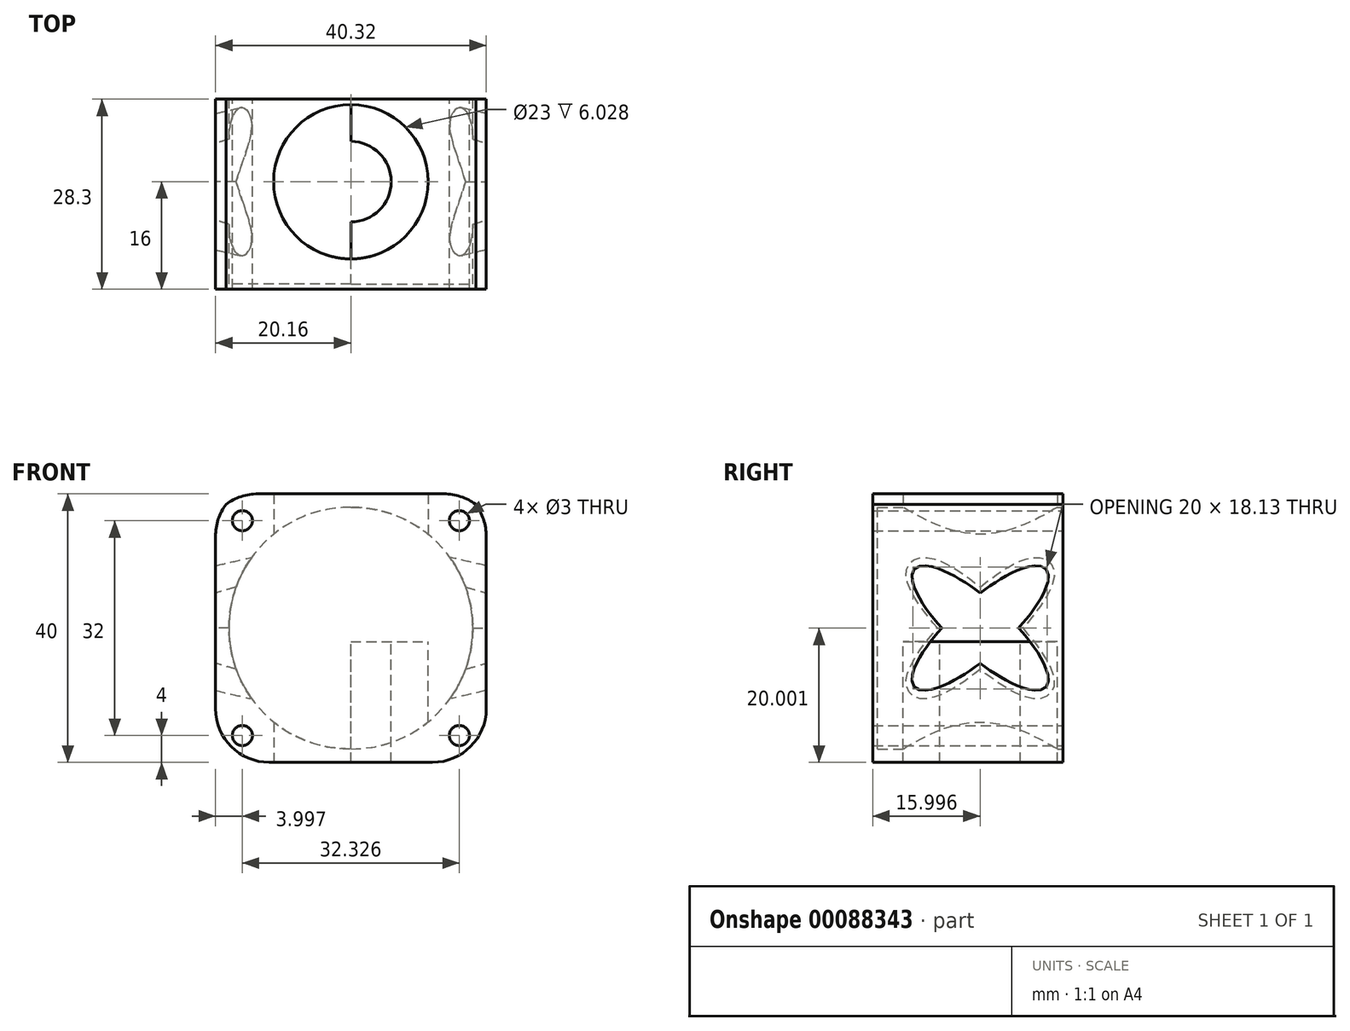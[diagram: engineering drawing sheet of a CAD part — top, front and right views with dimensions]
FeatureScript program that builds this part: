
annotation { "Feature Type Name" : "Feature", "Feature Type Description" : "" }
export const myFeature = defineFeature(function(context is Context, id is Id, definition is map)
    precondition{}
    {
        {
            var Q0;
            Q0=qCreatedBy(makeId("Top.planeOp"),FACE);
            var sketch = newSketch(context, id + "F11", { "sketchPlane" : qUnion([Q0])});
            skCircle(sketch, "E0", {"center": v(0, 0) * mm, "radius": 8 * mm});
            skCircle(sketch, "E1.cCircle", {"center": v(0, 0) * mm, "radius": 11.5 * mm, "construction": true});
            skLineSegment(sketch, "E1.0", {"start": v(11.5, 11.5) * mm, "end": v(11.5, -11.5) * mm});
            skLineSegment(sketch, "E1.1", {"start": v(11.5, -11.5) * mm, "end": v(-11.5, -11.5) * mm});
            skLineSegment(sketch, "E1.2", {"start": v(-11.5, -11.5) * mm, "end": v(-11.5, 11.5) * mm});
            skLineSegment(sketch, "E1.3", {"start": v(-11.5, 11.5) * mm, "end": v(11.5, 11.5) * mm});
            skPoint(sketch, "E1.0.midPoint", {"position": v(11.5, 0) * mm});
            skPoint(sketch, "E2.0.midPoint", {"position": v(0, 36.09) * mm});
            skPoint(sketch, "E3", {"position": v(0, -11.5) * mm});
            skLineSegment(sketch, "E4.MirrorCS", {"start": v(0, 12.3) * mm, "end": v(-20.16, 12.3) * mm});
            skLineSegment(sketch, "E5.MirrorCS", {"start": v(-20.16, 16) * mm, "end": v(-20.16, 0) * mm});
            skLineSegment(sketch, "E6.MirrorCS", {"start": v(0, -16) * mm, "end": v(-20.16, -16) * mm});
            skCircle(sketch, "E7", {"center": v(0, 0) * mm, "radius": 6 * mm});
            skCircle(sketch, "E8", {"center": v(0, 0) * mm, "radius": 11.5 * mm});
            skPoint(sketch, "E9.0.midPoint", {"position": v(0, -12.5) * mm});
            skLineSegment(sketch, "E10.0", {"start": v(-16.45, 9.5) * mm, "end": v(16.45, 9.5) * mm, "construction": true});
            skLineSegment(sketch, "E10.1", {"start": v(16.45, 9.5) * mm, "end": v(0, -19) * mm, "construction": true});
            skLineSegment(sketch, "E10.2", {"start": v(0, -19) * mm, "end": v(-16.45, 9.5) * mm, "construction": true});
            skPoint(sketch, "E10.0.midPoint", {"position": v(0, 9.5) * mm});
            skCircle(sketch, "E11", {"center": v(-16.45, 9.5) * mm, "radius": 1.5 * mm});
            skCircle(sketch, "E12", {"center": v(16.45, 9.5) * mm, "radius": 1.5 * mm});
            skCircle(sketch, "E13", {"center": v(0, -19) * mm, "radius": 1.5 * mm});
            skLineSegment(sketch, "E14", {"start": v(-20.16, 0) * mm, "end": v(-20.16, -16) * mm});
            skLineSegment(sketch, "E15", {"start": v(0, 12.3) * mm, "end": v(0, -16) * mm});
            skLineSegment(sketch, "E16.MirrorCS", {"start": v(0, 12.3) * mm, "end": v(20.16, 12.3) * mm});
            skLineSegment(sketch, "E17.MirrorCS", {"start": v(20.16, 16) * mm, "end": v(20.16, 0) * mm});
            skLineSegment(sketch, "E18.MirrorCS", {"start": v(20.16, 0) * mm, "end": v(20.16, -16) * mm});
            skLineSegment(sketch, "E19.MirrorCS", {"start": v(0, -16) * mm, "end": v(20.16, -16) * mm});
            skSolve(sketch);
        }
        {
            var Q0;
            {var subQ14=sQuery(id+"F11.wireOp",EDGE,"E4.MirrorCS");Q0=makeQuery(id+"F11.imprint","IMPRINT",FACE,{"disambiguationData":[TD([[makeQuery(id+"F11.imprint","IMPRINT",EDGE,{"derivedFrom":subQ14}),1.0]])]});}
            var Q1;
            Q1=makeQuery(id+"F11.imprint","IMPRINT",FACE,{"disambiguationData":[TD([[makeQuery(id+"F11.imprint","IMPRINT",EDGE,{"derivedFrom":sQuery(id+"F11.wireOp",EDGE,"E11")}),1.0]])]});
            var Q2;
            {var subQ0=sQuery(id+"F11.wireOp",EDGE,"E1.3");var subQ1=sQuery(id+"F11.wireOp",EDGE,"E1.2");var subQ2=makeQuery(id+"F11.imprint","INTERSECT",VERTEX,{"derivedFrom":[subQ1,subQ0]});Q2=makeQuery(id+"F11.imprint","IMPRINT",FACE,{"disambiguationData":[TD([[makeQuery(id+"F11.imprint","IMPRINT",EDGE,{"disambiguationData":[TD([[subQ2,1.0]])],"derivedFrom":subQ1}),-1.0]])]});}
            var Q3;
            {var subQ0=sQuery(id+"F11.wireOp",EDGE,"E1.2");var subQ1=sQuery(id+"F11.wireOp",EDGE,"E1.1");var subQ2=makeQuery(id+"F11.imprint","INTERSECT",VERTEX,{"derivedFrom":[subQ1,subQ0]});Q3=makeQuery(id+"F11.imprint","IMPRINT",FACE,{"disambiguationData":[TD([[makeQuery(id+"F11.imprint","IMPRINT",EDGE,{"disambiguationData":[TD([[subQ2,-1.0]])],"derivedFrom":subQ0}),-1.0]])]});}
            extrude(context, id + "F0", {"entities" : qUnion([Q0, Q1, Q2, Q3]), "depth" : 22 * mm});
        }
        {
            var Q0;
            {var subQ0=sQuery(id+"F11.wireOp",EDGE,"E1.3");var subQ1=sQuery(id+"F11.wireOp",EDGE,"E1.2");var subQ2=makeQuery(id+"F11.imprint","INTERSECT",VERTEX,{"derivedFrom":[subQ1,subQ0]});Q0=makeQuery(id+"F11.imprint","IMPRINT",FACE,{"disambiguationData":[TD([[makeQuery(id+"F11.imprint","IMPRINT",EDGE,{"disambiguationData":[TD([[subQ2,1.0]])],"derivedFrom":subQ1}),-1.0]])]});}
            var Q1;
            {var subQ14=sQuery(id+"F11.wireOp",EDGE,"E4.MirrorCS");Q1=makeQuery(id+"F11.imprint","IMPRINT",FACE,{"disambiguationData":[TD([[makeQuery(id+"F11.imprint","IMPRINT",EDGE,{"derivedFrom":subQ14}),1.0]])]});}
            var Q2;
            {var subQ0=sQuery(id+"F11.wireOp",EDGE,"E1.2");var subQ1=sQuery(id+"F11.wireOp",EDGE,"E1.1");var subQ2=makeQuery(id+"F11.imprint","INTERSECT",VERTEX,{"derivedFrom":[subQ1,subQ0]});Q2=makeQuery(id+"F11.imprint","IMPRINT",FACE,{"disambiguationData":[TD([[makeQuery(id+"F11.imprint","IMPRINT",EDGE,{"disambiguationData":[TD([[subQ2,-1.0]])],"derivedFrom":subQ0}),-1.0]])]});}
            var Q3;
            Q3=makeQuery(id+"F11.imprint","IMPRINT",FACE,{"disambiguationData":[TD([[makeQuery(id+"F11.imprint","IMPRINT",EDGE,{"derivedFrom":sQuery(id+"F11.wireOp",EDGE,"E11")}),1.0]])]});
            var Q4;
            {var subQ0=sQuery(id+"F11.wireOp",EDGE,"E15");var subQ1=sQuery(id+"F11.wireOp",EDGE,"E0");var subQ2=makeQuery(id+"F11.imprint","INTERSECT",VERTEX,{"disambiguationData":[OD(0.0)],"derivedFrom":[subQ1,subQ0]});Q4=makeQuery(id+"F11.imprint","IMPRINT",FACE,{"disambiguationData":[TD([[makeQuery(id+"F11.imprint","IMPRINT",EDGE,{"disambiguationData":[TD([[subQ2,-1.0]])],"derivedFrom":subQ1}),-1.0]])]});}
            var Q5;
            {var subQ0=sQuery(id+"F11.wireOp",EDGE,"E15");var subQ1=sQuery(id+"F11.wireOp",EDGE,"E0");var subQ2=makeQuery(id+"F11.imprint","INTERSECT",VERTEX,{"disambiguationData":[OD(0.0)],"derivedFrom":[subQ1,subQ0]});Q5=makeQuery(id+"F11.imprint","IMPRINT",FACE,{"disambiguationData":[TD([[makeQuery(id+"F11.imprint","IMPRINT",EDGE,{"disambiguationData":[TD([[subQ2,-1.0]])],"derivedFrom":subQ1}),1.0]])]});}
            extrude(context, id + "F1", {"entities" : qUnion([Q0, Q1, Q2, Q3, Q4, Q5]), "operationType" : NewBodyOperationType.ADD, "oppositeDirection" : true, "depth" : 18 * mm});
        }
        {
            var Q0;
            {var subQ0=sQuery(id+"F11.wireOp",EDGE,"E4.MirrorCS");var subQ1=sQuery(id+"F11.wireOp",EDGE,"b9b2a584-45d9-46e1-b681-84b6f52c41030.MirrorCS");Q0=makeQuery(id+"F1.boolean.opBoolean","MERGE",FACE,{"derivedFrom":[makeQuery(id+"F0.opExtrude","SWEPT_FACE",FACE,{"disambiguationData":[OSD([subQ1,subQ0])]}),makeQuery(id+"F1.opExtrude","SWEPT_FACE",FACE,{"disambiguationData":[OSD([subQ1,subQ0])]})]});}
            var sketch = newSketch(context, id + "F2", { "sketchPlane" : qUnion([Q0])});
            skLineSegment(sketch, "E20.bottom", {"start": v(20.16, 22) * mm, "end": v(20.16, 22) * mm});
            skLineSegment(sketch, "E20.top", {"start": v(20.16, -8) * mm, "end": v(20.16, -8) * mm});
            skLineSegment(sketch, "E20.left", {"start": v(20.16, 22) * mm, "end": v(20.16, -8) * mm});
            skLineSegment(sketch, "E20.right", {"start": v(20.16, 22) * mm, "end": v(20.16, -8) * mm});
            skCircle(sketch, "E21", {"center": v(0.16, 2) * mm, "radius": 18 * mm});
            skLineSegment(sketch, "E22.bottom", {"start": v(-15.84, -14) * mm, "end": v(16.16, -14) * mm, "construction": true});
            skLineSegment(sketch, "E22.top", {"start": v(-15.84, 18) * mm, "end": v(16.16, 18) * mm, "construction": true});
            skLineSegment(sketch, "E22.left", {"start": v(-15.84, -14) * mm, "end": v(-15.84, 18) * mm, "construction": true});
            skLineSegment(sketch, "E22.right", {"start": v(16.16, -14) * mm, "end": v(16.16, 18) * mm, "construction": true});
            skCircle(sketch, "E23", {"center": v(16.16, -14) * mm, "radius": 1.5 * mm});
            skCircle(sketch, "E24", {"center": v(-15.84, -14) * mm, "radius": 1.5 * mm});
            skCircle(sketch, "E25", {"center": v(-15.84, 18) * mm, "radius": 1.5 * mm});
            skCircle(sketch, "E26", {"center": v(16.16, 18) * mm, "radius": 1.5 * mm});
            skSolve(sketch);
        }
        {
            var Q0;
            {var subQ0=sQuery(id+"F2.wireOp",EDGE,"E21");var subQ1=sQuery(id+"F11.wireOp",EDGE,"E16.MirrorCS");var subQ2=sQuery(id+"F11.wireOp",EDGE,"E15");var subQ3=sQuery(id+"F11.wireOp",EDGE,"E4.MirrorCS");var subQ4=makeQuery(id+"F1.boolean.opBoolean","MERGE",EDGE,{"derivedFrom":[makeQuery(id+"F0.opExtrude","SWEPT_EDGE",EDGE,{"disambiguationData":[OSD([subQ3,subQ2,subQ1])]}),makeQuery(id+"F1.opExtrude","SWEPT_EDGE",EDGE,{"disambiguationData":[OSD([subQ3,subQ2,subQ1])]})]});var subQ5=makeQuery(id+"F2.imprint","INTERSECT",VERTEX,{"disambiguationData":[OD(0.0)],"derivedFrom":[subQ4,subQ0]});Q0=makeQuery(id+"F2.imprint","IMPRINT",FACE,{"disambiguationData":[TD([[makeQuery(id+"F2.imprint","IMPRINT",EDGE,{"disambiguationData":[TD([[subQ5,1.0]])],"derivedFrom":subQ0}),1.0]])]});}
            var Q1;
            Q1=makeQuery(id+"F2.imprint","IMPRINT",FACE,{"disambiguationData":[TD([[makeQuery(id+"F2.imprint","IMPRINT",EDGE,{"derivedFrom":sQuery(id+"F2.wireOp",EDGE,"E23")}),1.0]])]});
            var Q2;
            Q2=makeQuery(id+"F2.imprint","IMPRINT",FACE,{"disambiguationData":[TD([[makeQuery(id+"F2.imprint","IMPRINT",EDGE,{"derivedFrom":sQuery(id+"F2.wireOp",EDGE,"E26")}),1.0]])]});
            extrude(context, id + "F3", {"entities" : qUnion([Q0, Q1, Q2]), "operationType" : NewBodyOperationType.REMOVE, "oppositeDirection" : true, "depth" : 27.57 * mm});
        }
        {
            var Q0;
            Q0=makeQuery(id+"F2.imprint","IMPRINT",FACE,{"disambiguationData":[TD([[makeQuery(id+"F2.imprint","IMPRINT",EDGE,{"derivedFrom":sQuery(id+"F2.wireOp",EDGE,"E23")}),1.0]])]});
            var Q1;
            Q1=makeQuery(id+"F2.imprint","IMPRINT",FACE,{"disambiguationData":[TD([[makeQuery(id+"F2.imprint","IMPRINT",EDGE,{"derivedFrom":sQuery(id+"F2.wireOp",EDGE,"E24")}),1.0]])]});
            var Q2;
            Q2=makeQuery(id+"F2.imprint","IMPRINT",FACE,{"disambiguationData":[TD([[makeQuery(id+"F2.imprint","IMPRINT",EDGE,{"derivedFrom":sQuery(id+"F2.wireOp",EDGE,"E26")}),1.0]])]});
            var Q3;
            Q3=makeQuery(id+"F2.imprint","IMPRINT",FACE,{"disambiguationData":[TD([[makeQuery(id+"F2.imprint","IMPRINT",EDGE,{"derivedFrom":sQuery(id+"F2.wireOp",EDGE,"E25")}),1.0]])]});
            extrude(context, id + "F4", {"entities" : qUnion([Q0, Q1, Q2, Q3]), "operationType" : NewBodyOperationType.REMOVE, "oppositeDirection" : true, "depth" : 50 * mm});
        }
        {
            var Q0;
            {var subQ0=sQuery(id+"F11.wireOp",EDGE,"E15");var subQ1=sQuery(id+"F11.wireOp",EDGE,"E0");var subQ2=makeQuery(id+"F11.imprint","INTERSECT",VERTEX,{"disambiguationData":[OD(0.0)],"derivedFrom":[subQ1,subQ0]});Q0=makeQuery(id+"F11.imprint","IMPRINT",FACE,{"disambiguationData":[TD([[makeQuery(id+"F11.imprint","IMPRINT",EDGE,{"disambiguationData":[TD([[subQ2,-1.0]])],"derivedFrom":subQ1}),1.0]])]});}
            extrude(context, id + "F5", {"entities" : qUnion([Q0]), "operationType" : NewBodyOperationType.ADD, "oppositeDirection" : true, "depth" : 16.75 * mm, "hasSecondDirection" : true, "secondDirectionOppositeDirection" : true, "secondDirectionDepth" : 12.5 * mm});
        }
        {
            var Q0;
            {var subQ0=sQuery(id+"F11.wireOp",EDGE,"E14");var subQ1=sQuery(id+"F11.wireOp",EDGE,"E5.MirrorCS");Q0=makeQuery(id+"F1.boolean.opBoolean","MERGE",FACE,{"derivedFrom":[makeQuery(id+"F0.opExtrude","SWEPT_FACE",FACE,{"disambiguationData":[OSD([subQ1,subQ0])]}),makeQuery(id+"F1.opExtrude","SWEPT_FACE",FACE,{"disambiguationData":[OSD([subQ1,subQ0])]})]});}
            var sketch = newSketch(context, id + "F6", { "sketchPlane" : qUnion([Q0])});
            skLineSegment(sketch, "E27", {"start": v(1.85, -18) * mm, "end": v(1.85, 22) * mm});
            skEllipticalArc(sketch, "E28", {});
            skEllipticalArc(sketch, "E29.MirrorC", {});
            skEllipticalArc(sketch, "E30.trimOffspring", {});
            skEllipticalArc(sketch, "E31.trimOffspring", {});
            const initialGuessF6  = {"E28": [0, 0.002, 0.7439449466811624, -0.668240911878016, 0.013163284631340309, 0.004040661274424356, 1.8398389710414638, 4.383091535645527], "E29.MirrorC": [0, 0.002, -0.7439449466811624, -0.668240911878016, 0.013163284631340309, 0.004040661274424356, 1.9000937715340587, 4.443346336138123], "E30.trimOffspring": [0, 0.002, 0.7439449466811624, -0.668240911878016, 0.013163284631340309, 0.004040661274424356, 4.981431624631257, 1.2414988820557344], "E31.trimOffspring": [0, 0.002, -0.7439449466811624, -0.668240911878016, 0.013163284631340309, 0.004040661274424356, 5.041686425123852, 1.3017536825483293]};
            skSetInitialGuess(sketch, initialGuessF6);
            skSolve(sketch);
        }
        {
            var Q0;
            Q0=qSketchRegion(id+"F6",true);
            extrude(context, id + "F7", {"entities" : qUnion([Q0]), "operationType" : NewBodyOperationType.REMOVE, "oppositeDirection" : true, "depth" : 18 * mm, "hasDraft" : true, "draftAngle" : 13 * degree});
        }
        {
            var Q0;
            Q0=makeQuery(id+"F0.opExtrude","CAP_EDGE",EDGE,{"disambiguationData":[OSD([sQuery(id+"F11.wireOp",EDGE,"E5.MirrorCS"),sQuery(id+"F11.wireOp",EDGE,"E14")])],"isStart":false});
            chamfer(context, id + "F8", {"entities" : qUnion([Q0]), "width" : 3 * mm, "tangentPropagation" : true});
        }
        {
            var Q0;
            Q0=makeQuery(id+"F1.opExtrude","CAP_EDGE",EDGE,{"disambiguationData":[OSD([sQuery(id+"F11.wireOp",EDGE,"E5.MirrorCS"),sQuery(id+"F11.wireOp",EDGE,"E14")])],"isStart":false});
            var Q1;
            {var subQ0=sQuery(id+"F11.wireOp",EDGE,"E14");var subQ1=sQuery(id+"F11.wireOp",EDGE,"E5.MirrorCS");Q1=makeQuery(id+"F8.opChamfer","BLEND_EDGE",EDGE,{"blendedFrom":[makeQuery(id+"F0.opExtrude","CAP_EDGE",EDGE,{"disambiguationData":[OSD([subQ1,subQ0])],"isStart":false}),makeQuery(id+"F1.boolean.opBoolean","MERGE",FACE,{"derivedFrom":[makeQuery(id+"F0.opExtrude","SWEPT_FACE",FACE,{"disambiguationData":[OSD([subQ1,subQ0])]}),makeQuery(id+"F1.opExtrude","SWEPT_FACE",FACE,{"disambiguationData":[OSD([subQ1,subQ0])]})]})],"blendedInto":[makeQuery(id+"F1.boolean.opBoolean","MERGE",FACE,{"derivedFrom":[makeQuery(id+"F0.opExtrude","SWEPT_FACE",FACE,{"disambiguationData":[OSD([subQ1,subQ0])]}),makeQuery(id+"F1.opExtrude","SWEPT_FACE",FACE,{"disambiguationData":[OSD([subQ1,subQ0])]})]})]});}
            var Q2;
            {var subQ0=sQuery(id+"F11.wireOp",EDGE,"E14");var subQ1=sQuery(id+"F11.wireOp",EDGE,"E5.MirrorCS");Q2=makeQuery(id+"F8.opChamfer","BLEND_EDGE",EDGE,{"blendedFrom":[makeQuery(id+"F0.opExtrude","CAP_EDGE",EDGE,{"disambiguationData":[OSD([subQ1,subQ0])],"isStart":false}),makeQuery(id+"F0.opExtrude","CAP_FACE",FACE,{"disambiguationData":[OSD([sQuery(id+"F11.wireOp",EDGE,"E0"),sQuery(id+"F11.wireOp",EDGE,"E4.MirrorCS"),subQ1,sQuery(id+"F11.wireOp",EDGE,"E6.MirrorCS"),subQ0,sQuery(id+"F11.wireOp",EDGE,"oFPHxFXu-qfng-hnN3-3d4T-xQRbBp33RM5M")])],"isStart":false})],"blendedInto":[makeQuery(id+"F0.opExtrude","CAP_FACE",FACE,{"disambiguationData":[OSD([sQuery(id+"F11.wireOp",EDGE,"E0"),sQuery(id+"F11.wireOp",EDGE,"E4.MirrorCS"),subQ1,sQuery(id+"F11.wireOp",EDGE,"E6.MirrorCS"),subQ0,sQuery(id+"F11.wireOp",EDGE,"oFPHxFXu-qfng-hnN3-3d4T-xQRbBp33RM5M")])],"isStart":false})]});}
            fillet(context, id + "F9", {"entities" : qUnion([Q0, Q1, Q2]), "radius" : 8 * mm, "tangentPropagation" : true, "allowEdgeOverflow" : false});
        }
        {
            var Q0;
            Q0=makeQuery(id+"F0.opExtrude","SWEPT_BODY",BODY,{"disambiguationData":[OSD([sQuery(id+"F11.wireOp",EDGE,"E4.MirrorCS"),sQuery(id+"F11.wireOp",EDGE,"E5.MirrorCS"),sQuery(id+"F11.wireOp",EDGE,"E6.MirrorCS"),sQuery(id+"F11.wireOp",EDGE,"E8"),sQuery(id+"F11.wireOp",EDGE,"E14"),sQuery(id+"F11.wireOp",EDGE,"E15")])]});
            var Q1;
            {var subQ0=sQuery(id+"F11.wireOp",EDGE,"E15");var subQ1=makeQuery(id+"F11.imprint","INTERSECT",VERTEX,{"disambiguationData":[OD(1.0)],"derivedFrom":[sQuery(id+"F11.wireOp",EDGE,"E0"),subQ0]});var subQ2=makeQuery(id+"F11.imprint","IMPRINT",EDGE,{"disambiguationData":[TD([[subQ1,1.0]])],"derivedFrom":subQ0});var subQ4=makeQuery(id+"F11.imprint","IMPRINT",EDGE,{"disambiguationData":[TD([[makeQuery(id+"F11.imprint","INTERSECT",VERTEX,{"derivedFrom":[sQuery(id+"F11.wireOp",EDGE,"E6.MirrorCS"),subQ0,sQuery(id+"F11.wireOp",EDGE,"E19.MirrorCS")]}),1.0]])],"derivedFrom":subQ0});Q1=makeQuery(id+"F5.boolean.opBoolean","MERGE",FACE,{"derivedFrom":[makeQuery(id+"F1.boolean.opBoolean","MERGE",FACE,{"derivedFrom":[makeQuery(id+"F0.opExtrude","SWEPT_FACE",FACE,{"disambiguationData":[OSD([subQ0]),TDD([subQ4])]}),makeQuery(id+"F1.opExtrude","SWEPT_FACE",FACE,{"disambiguationData":[OSD([subQ0]),TDD([subQ2,makeQuery(id+"F11.imprint","IMPRINT",EDGE,{"disambiguationData":[TD([[subQ1,-1.0]])],"derivedFrom":subQ0}),subQ4])]})]}),makeQuery(id+"F5.opExtrude","SWEPT_FACE",FACE,{"disambiguationData":[OSD([subQ0]),TDD([subQ2])]})]});}
            mirror(context, id + "F10", {"operationType" : NewBodyOperationType.ADD, "entities" : qUnion([Q0]), "mirrorPlane" : qUnion([Q1])});
        }
    });
